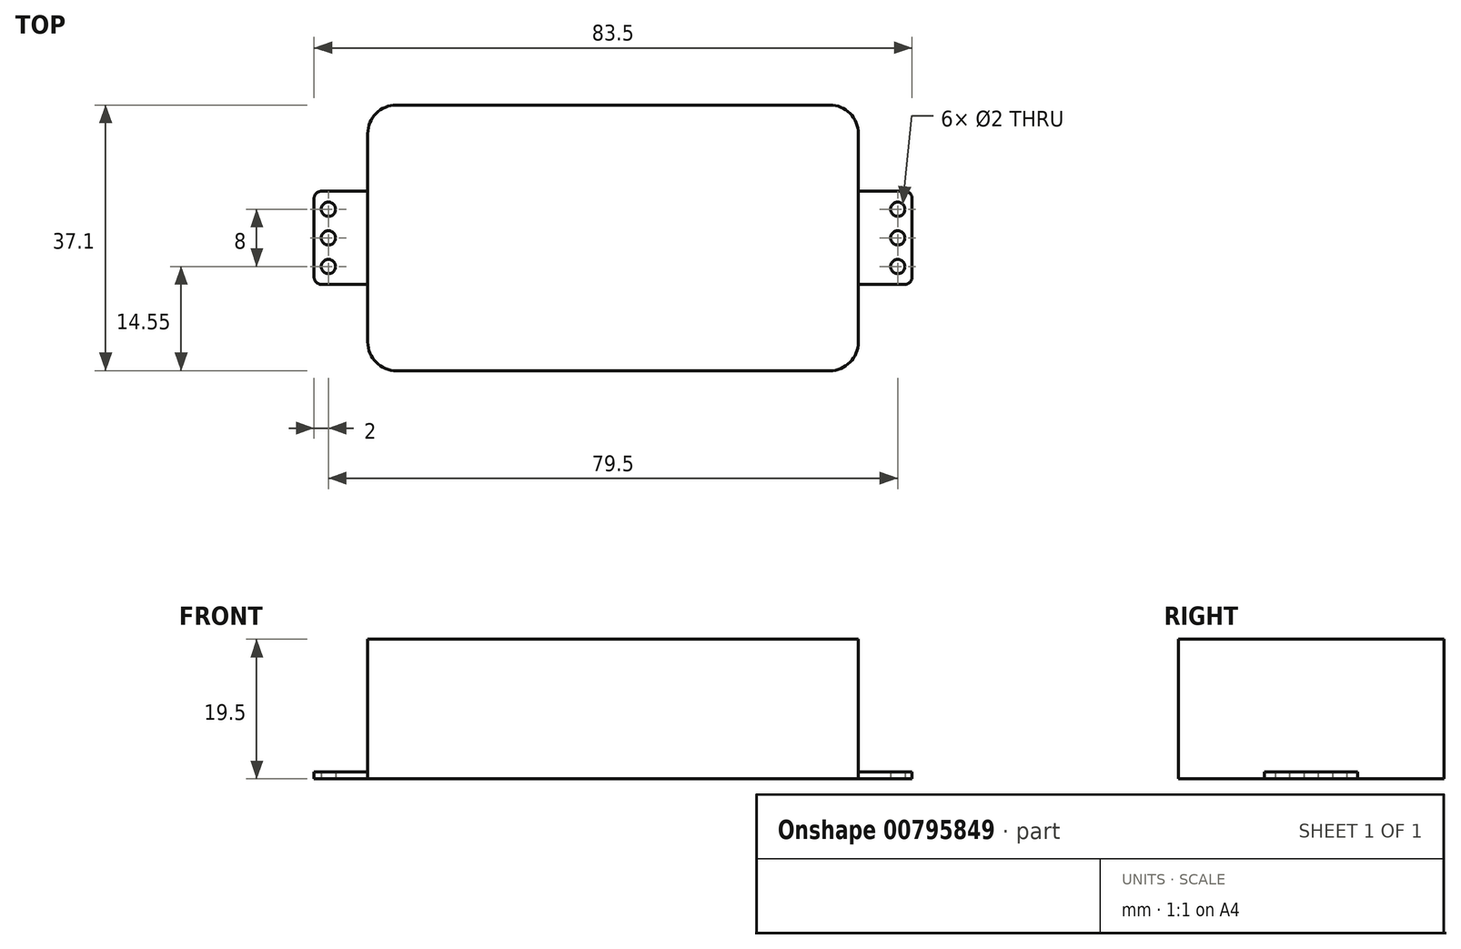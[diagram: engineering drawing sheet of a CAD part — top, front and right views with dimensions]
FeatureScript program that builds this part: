
annotation { "Feature Type Name" : "Feature", "Feature Type Description" : "" }
export const myFeature = defineFeature(function(context is Context, id is Id, definition is map)
    precondition{}
    {
        {
            var Q0;
            Q0=qCreatedBy(makeId("Top.planeOp"),FACE);
            var sketch = newSketch(context, id + "F0", { "sketchPlane" : qUnion([Q0])});
            skLineSegment(sketch, "E0.bottom", {"start": v(-41.75, 18.55) * mm, "end": v(41.75, 18.55) * mm, "construction": true});
            skLineSegment(sketch, "E0.top", {"start": v(-41.75, -18.55) * mm, "end": v(41.75, -18.55) * mm, "construction": true});
            skLineSegment(sketch, "E0.left", {"start": v(-41.75, 18.55) * mm, "end": v(-41.75, -18.55) * mm, "construction": true});
            skLineSegment(sketch, "E0.right", {"start": v(41.75, 18.55) * mm, "end": v(41.75, -18.55) * mm, "construction": true});
            skLineSegment(sketch, "E1.bottom", {"start": v(-30.25, 18.55) * mm, "end": v(30.25, 18.55) * mm});
            skLineSegment(sketch, "E1.top", {"start": v(-30.25, -18.55) * mm, "end": v(30.25, -18.55) * mm});
            skLineSegment(sketch, "E1.left", {"start": v(-34.25, 14.55) * mm, "end": v(-34.25, -14.55) * mm});
            skLineSegment(sketch, "E1.right", {"start": v(34.25, 14.55) * mm, "end": v(34.25, -14.55) * mm});
            skPoint(sketch, "E2.visualSharp", {"position": v(-34.25, 18.55) * mm});
            skArc(sketch, "E2.filletArc", {"start": v(-30.25, 18.55) * mm, "mid": v(-33.08, 17.38) * mm, "end": v(-34.25, 14.55) * mm});
            skPoint(sketch, "E3.visualSharp", {"position": v(-34.25, -18.55) * mm});
            skArc(sketch, "E3.filletArc", {"start": v(-34.25, -14.55) * mm, "mid": v(-33.08, -17.38) * mm, "end": v(-30.25, -18.55) * mm});
            skPoint(sketch, "E4.visualSharp", {"position": v(34.25, 18.55) * mm});
            skArc(sketch, "E4.filletArc", {"start": v(34.25, 14.55) * mm, "mid": v(33.08, 17.38) * mm, "end": v(30.25, 18.55) * mm});
            skPoint(sketch, "E5.visualSharp", {"position": v(34.25, -18.55) * mm});
            skArc(sketch, "E5.filletArc", {"start": v(30.25, -18.55) * mm, "mid": v(33.08, -17.38) * mm, "end": v(34.25, -14.55) * mm});
            skLineSegment(sketch, "E6.bottom", {"start": v(-40.75, 6.5) * mm, "end": v(-34.25, 6.5) * mm});
            skLineSegment(sketch, "E6.top", {"start": v(-40.75, -6.5) * mm, "end": v(-34.25, -6.5) * mm});
            skLineSegment(sketch, "E6.left", {"start": v(-41.75, 5.5) * mm, "end": v(-41.75, -5.5) * mm});
            skLineSegment(sketch, "E6.right", {"start": v(-34.25, 6.5) * mm, "end": v(-34.25, -6.5) * mm});
            skLineSegment(sketch, "E7.bottom", {"start": v(34.25, 6.5) * mm, "end": v(40.75, 6.5) * mm});
            skLineSegment(sketch, "E7.top", {"start": v(34.25, -6.5) * mm, "end": v(40.75, -6.5) * mm});
            skLineSegment(sketch, "E7.left", {"start": v(34.25, 6.5) * mm, "end": v(34.25, -6.5) * mm});
            skLineSegment(sketch, "E7.right", {"start": v(41.75, 5.5) * mm, "end": v(41.75, -5.5) * mm});
            skPoint(sketch, "E8.visualSharp", {"position": v(-41.75, 6.5) * mm});
            skArc(sketch, "E8.filletArc", {"start": v(-40.75, 6.5) * mm, "mid": v(-41.46, 6.2) * mm, "end": v(-41.75, 5.5) * mm});
            skPoint(sketch, "E9.visualSharp", {"position": v(-41.75, -6.5) * mm});
            skArc(sketch, "E9.filletArc", {"start": v(-41.75, -5.5) * mm, "mid": v(-41.46, -6.2) * mm, "end": v(-40.75, -6.5) * mm});
            skPoint(sketch, "E10.visualSharp", {"position": v(41.75, 6.5) * mm});
            skArc(sketch, "E10.filletArc", {"start": v(41.75, 5.5) * mm, "mid": v(41.46, 6.2) * mm, "end": v(40.75, 6.5) * mm});
            skPoint(sketch, "E11.visualSharp", {"position": v(41.75, -6.5) * mm});
            skArc(sketch, "E11.filletArc", {"start": v(40.75, -6.5) * mm, "mid": v(41.46, -6.2) * mm, "end": v(41.75, -5.5) * mm});
            skCircle(sketch, "E12", {"center": v(-39.75, 4) * mm, "radius": 1 * mm});
            skCircle(sketch, "E13", {"center": v(-39.75, 0) * mm, "radius": 1 * mm});
            skCircle(sketch, "E14", {"center": v(-39.75, -4) * mm, "radius": 1 * mm});
            skLineSegment(sketch, "E15", {"start": v(-39.75, 4) * mm, "end": v(-39.75, -4) * mm, "construction": true});
            skCircle(sketch, "E16.MirrorC", {"center": v(39.75, -4) * mm, "radius": 1 * mm});
            skCircle(sketch, "E17.MirrorC", {"center": v(39.75, 0) * mm, "radius": 1 * mm});
            skCircle(sketch, "E18.MirrorC", {"center": v(39.75, 4) * mm, "radius": 1 * mm});
            skSolve(sketch);
        }
        {
            var Q0;
            Q0 = qSketchRegion(id + "F0", true);
            extrude(context, id + "F1", {"entities" : qUnion([Q0]), "depth" : 19.5 * mm, "offsetDistance" : 25 * mm});
        }
        {
            var Q0;
            Q0=qCreatedBy(makeId("Front.planeOp"),FACE);
            var sketch = newSketch(context, id + "F2", { "sketchPlane" : qUnion([Q0])});
            skLineSegment(sketch, "E19", {"start": v(-34.25, 1) * mm, "end": v(-41.75, 1) * mm});
            skLineSegment(sketch, "E20", {"start": v(-41.75, 1) * mm, "end": v(-41.75, 19.5) * mm});
            skLineSegment(sketch, "E21", {"start": v(-41.75, 19.5) * mm, "end": v(-34.25, 19.5) * mm});
            skLineSegment(sketch, "E22", {"start": v(-34.25, 19.5) * mm, "end": v(-34.25, 1) * mm});
            skLineSegment(sketch, "E23.MirrorCS", {"start": v(34.25, 1) * mm, "end": v(41.75, 1) * mm});
            skLineSegment(sketch, "E24.MirrorCS", {"start": v(34.25, 19.5) * mm, "end": v(34.25, 1) * mm});
            skLineSegment(sketch, "E25.MirrorCS", {"start": v(41.75, 19.5) * mm, "end": v(34.25, 19.5) * mm});
            skLineSegment(sketch, "E26.MirrorCS", {"start": v(41.75, 1) * mm, "end": v(41.75, 19.5) * mm});
            skSolve(sketch);
        }
        {
            var Q0;
            Q0 = qSketchRegion(id + "F2", true);
            extrude(context, id + "F3", {"entities" : qUnion([Q0]), "operationType" : NewBodyOperationType.REMOVE, "endBound" : BoundingType.SYMMETRIC, "oppositeDirection" : true, "depth" : 25 * mm, "offsetDistance" : 25 * mm});
        }
    });
